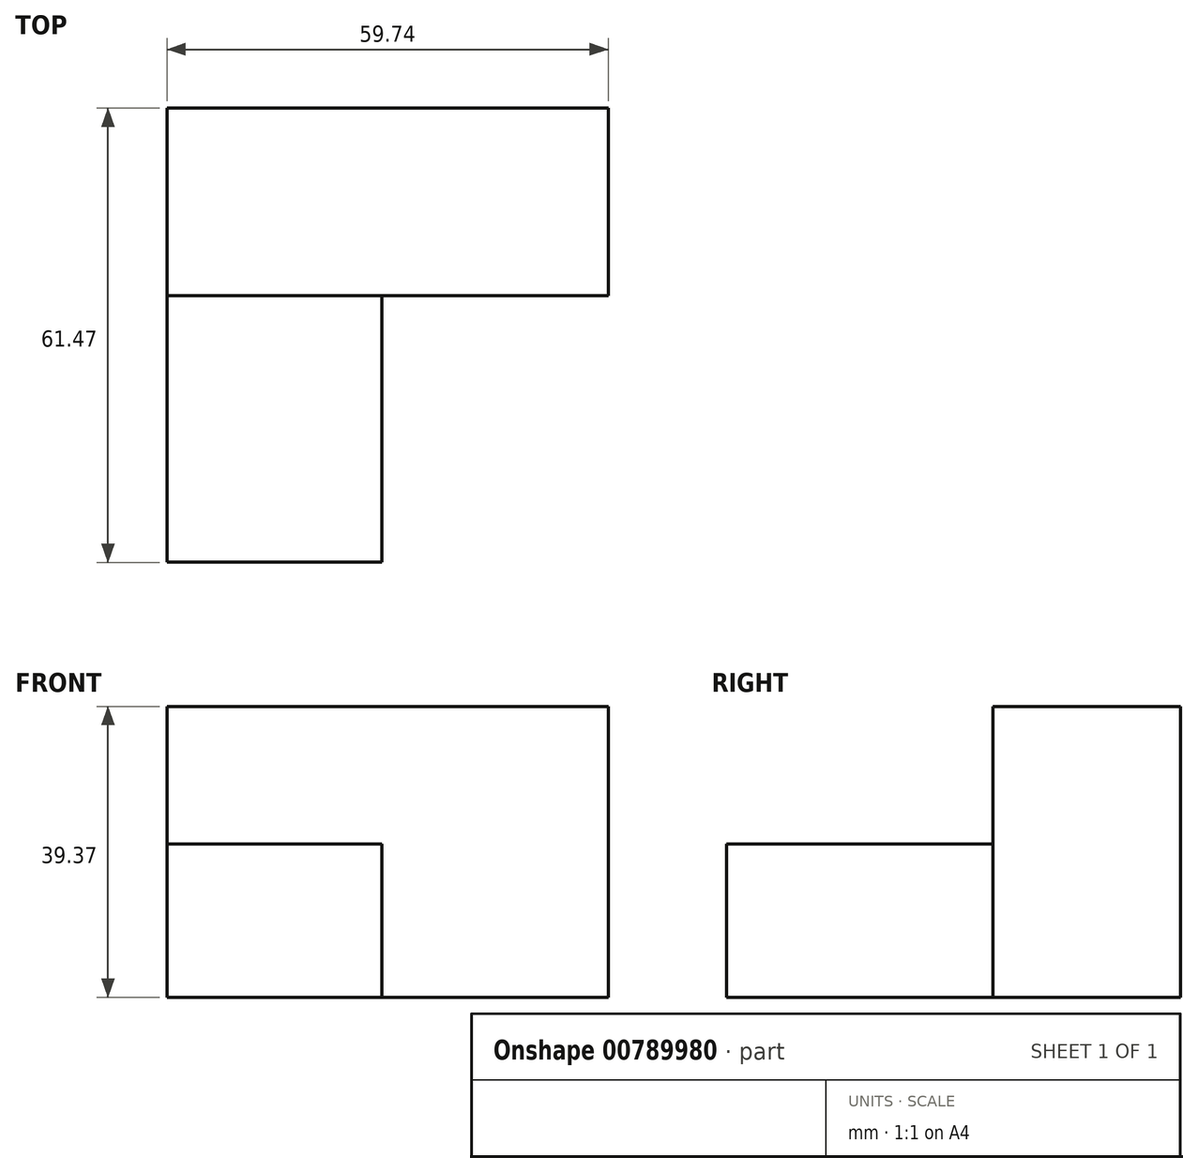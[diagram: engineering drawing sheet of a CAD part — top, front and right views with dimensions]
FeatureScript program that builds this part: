
annotation { "Feature Type Name" : "Feature", "Feature Type Description" : "" }
export const myFeature = defineFeature(function(context is Context, id is Id, definition is map)
    precondition{}
    {
        {
            var Q0;
            Q0=qCreatedBy(makeId("Front.planeOp"),FACE);
            var sketch = newSketch(context, id + "F0", { "sketchPlane" : qUnion([Q0])});
            skLineSegment(sketch, "E0", {"start": v(0, 0) * mm, "end": v(0, 20.76) * mm});
            skLineSegment(sketch, "E1", {"start": v(0, 20.76) * mm, "end": v(-29.09, 20.76) * mm});
            skLineSegment(sketch, "E2", {"start": v(-29.09, 20.76) * mm, "end": v(-29.09, 0) * mm});
            skLineSegment(sketch, "E3", {"start": v(-29.09, 0) * mm, "end": v(0, 0) * mm});
            skLineSegment(sketch, "E4", {"start": v(-29.09, 20.76) * mm, "end": v(-29.09, 39.37) * mm});
            skLineSegment(sketch, "E5", {"start": v(-29.09, 39.37) * mm, "end": v(30.65, 39.37) * mm});
            skLineSegment(sketch, "E6", {"start": v(30.65, 39.37) * mm, "end": v(30.65, 0) * mm});
            skLineSegment(sketch, "E7", {"start": v(30.65, 0) * mm, "end": v(0, 0) * mm});
            skSolve(sketch);
        }
        {
            var Q0;
            Q0=makeQuery(id+"F0.imprint","IMPRINT",FACE,{"disambiguationData":[TD([[makeQuery(id+"F0.imprint","IMPRINT",EDGE,{"derivedFrom":sQuery(id+"F0.wireOp",EDGE,"E0")}),1.0]])]});
            extrude(context, id + "F1", {"entities" : qUnion([Q0]), "depth" : 48.77 * mm, "offsetDistance" : 25.4 * mm});
        }
        {
            var Q0;
            Q0 = qSketchRegion(id + "F0", true);
            extrude(context, id + "F2", {"entities" : qUnion([Q0]), "operationType" : NewBodyOperationType.ADD, "endBound" : BoundingType.SYMMETRIC, "depth" : 25.4 * mm, "offsetDistance" : 25.4 * mm});
        }
    });
